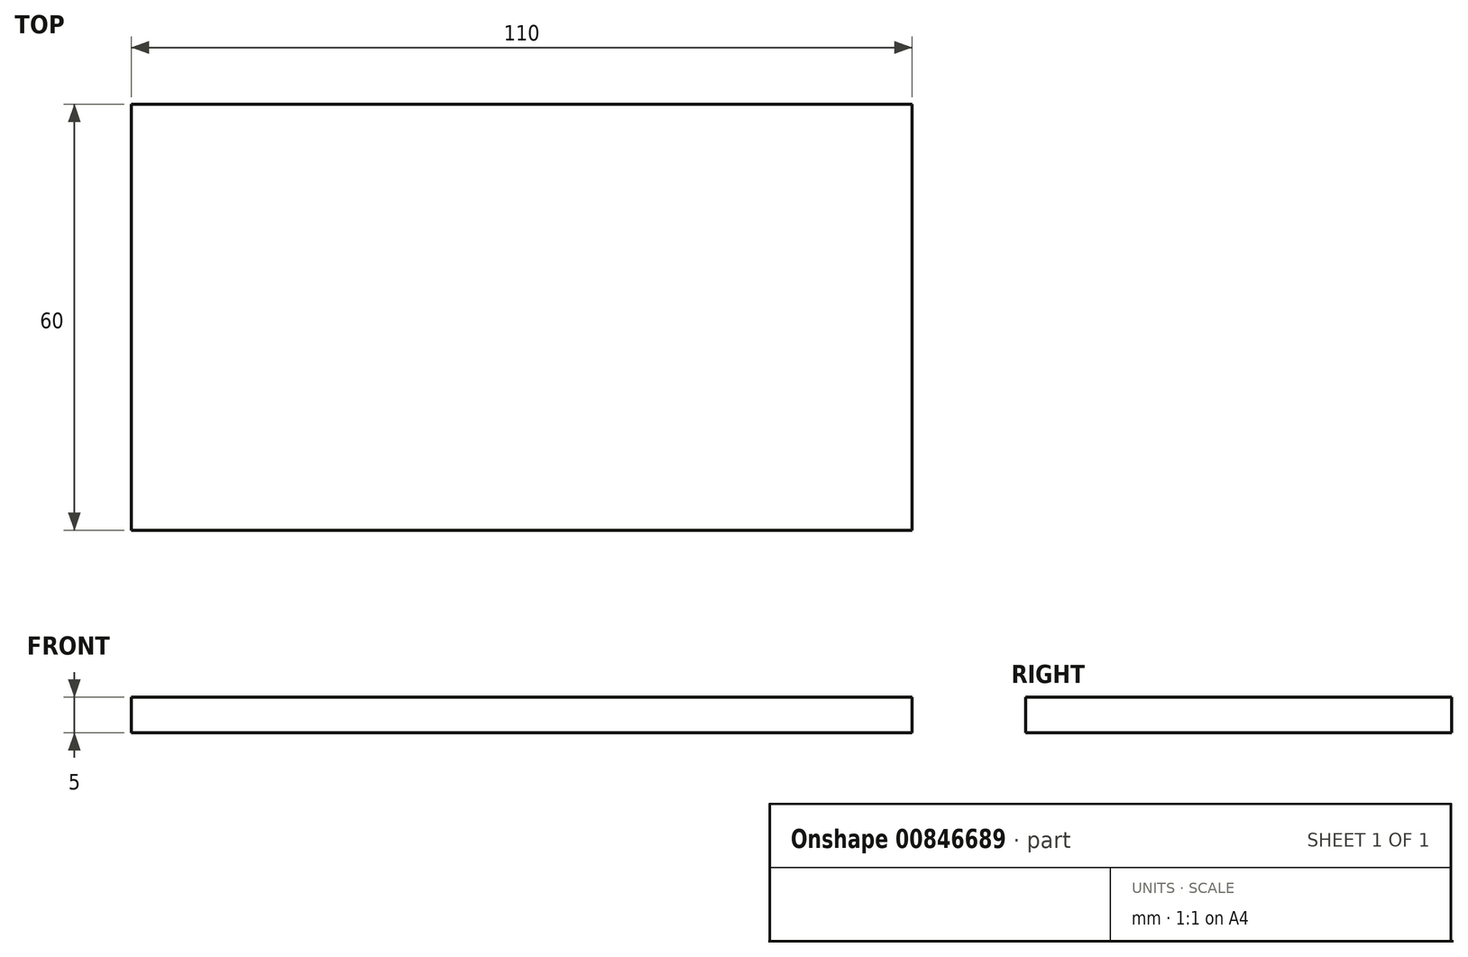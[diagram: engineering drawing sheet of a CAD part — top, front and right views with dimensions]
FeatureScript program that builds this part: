
annotation { "Feature Type Name" : "Feature", "Feature Type Description" : "" }
export const myFeature = defineFeature(function(context is Context, id is Id, definition is map)
    precondition{}
    {
        {
            var Q0;
            Q0=qCreatedBy(makeId("Top.planeOp"),FACE);
            var sketch = newSketch(context, id + "F0", { "sketchPlane" : qUnion([Q0])});
            skLineSegment(sketch, "E0.bottom", {"start": v(-67.47, 21.66) * mm, "end": v(42.53, 21.66) * mm});
            skLineSegment(sketch, "E0.top", {"start": v(-67.47, -38.34) * mm, "end": v(42.53, -38.34) * mm});
            skLineSegment(sketch, "E0.left", {"start": v(-67.47, 21.66) * mm, "end": v(-67.47, -38.34) * mm});
            skLineSegment(sketch, "E0.right", {"start": v(42.53, 21.66) * mm, "end": v(42.53, -38.34) * mm});
            skSolve(sketch);
        }
        {
            var Q0;
            Q0 = qSketchRegion(id + "F0", true);
            extrude(context, id + "F1", {"entities" : qUnion([Q0]), "depth" : 5 * mm, "offsetDistance" : 25 * mm});
        }
    });
